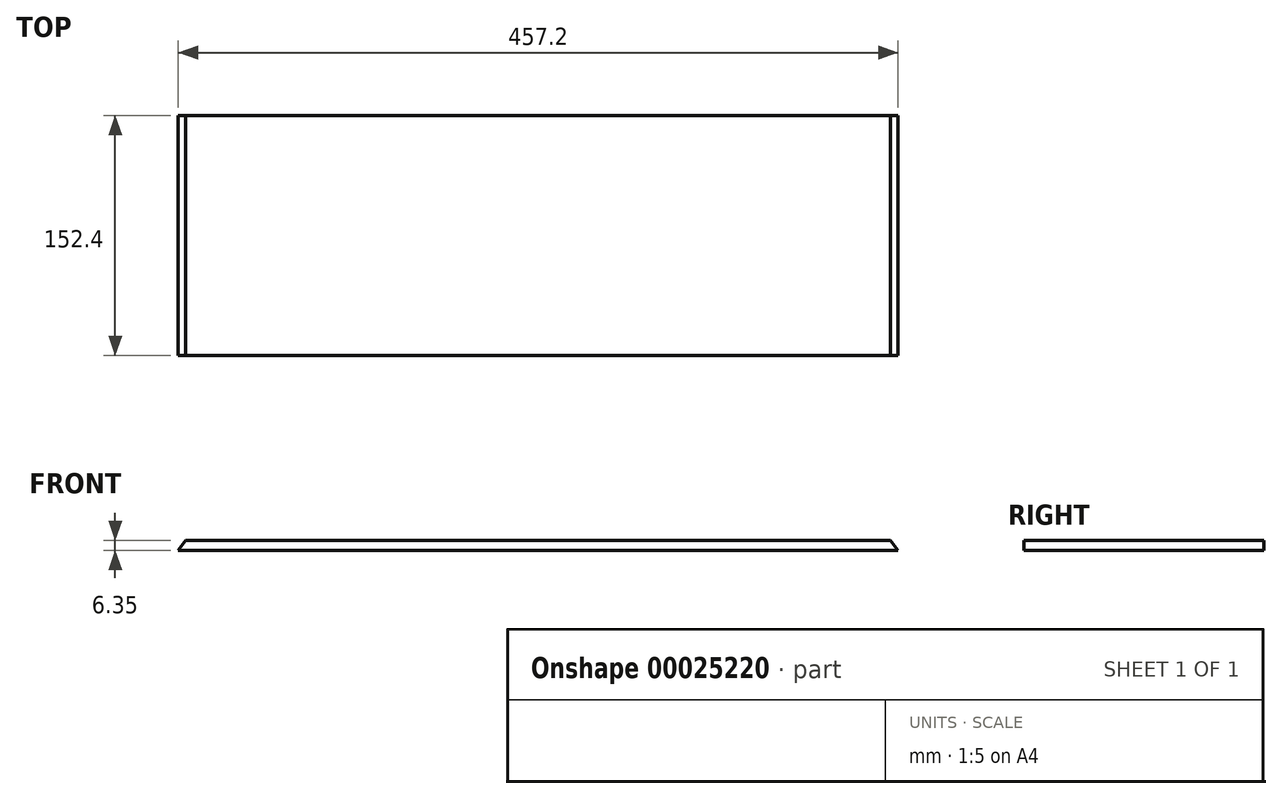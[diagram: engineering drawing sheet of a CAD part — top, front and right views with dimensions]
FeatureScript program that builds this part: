
annotation { "Feature Type Name" : "Feature", "Feature Type Description" : "" }
export const myFeature = defineFeature(function(context is Context, id is Id, definition is map)
    precondition{}
    {
        {
            var Q0;
            Q0=qCreatedBy(makeId("Front.planeOp"),FACE);
            var sketch = newSketch(context, id + "F0", { "sketchPlane" : qUnion([Q0])});
            skLineSegment(sketch, "E0.bottom", {"start": v(0, 0) * mm, "end": v(457.2, 0) * mm});
            skPoint(sketch, "E1", {"position": v(228.6, 0) * mm});
            skLineSegment(sketch, "E2", {"start": v(228.6, 0) * mm, "end": v(228.6, 6.35) * mm});
            skLineSegment(sketch, "E3", {"start": v(228.6, 6.35) * mm, "end": v(4.76, 6.35) * mm});
            skLineSegment(sketch, "E4", {"start": v(0, 0) * mm, "end": v(4.76, 6.35) * mm});
            skLineSegment(sketch, "E5.MirrorCS", {"start": v(228.6, 6.35) * mm, "end": v(452.44, 6.35) * mm});
            skLineSegment(sketch, "E6.MirrorCS", {"start": v(457.2, 0) * mm, "end": v(452.44, 6.35) * mm});
            skSolve(sketch);
        }
        {
            var Q0;
            Q0 = qSketchRegion(id + "F0", true);
            extrude(context, id + "F1", {"entities" : qUnion([Q0]), "depth" : 152.4 * mm});
        }
    });
